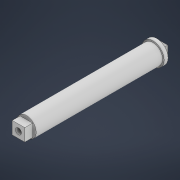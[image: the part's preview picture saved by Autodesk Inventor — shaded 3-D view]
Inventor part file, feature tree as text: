
AUTODESK INVENTOR PART (.ipt)
format: ipt  version: 2021 (Build 250183000, 183)  size: 122,880 bytes
history: native  units: mm
features: extrude x6, sketch x6
ambient origin geometry x8: Origin, YZ Plane, XZ Plane, XY Plane, X Axis, Y Axis, Z Axis, Center Point
bodies: Volumenkörper1 (feature_tree)
feature tree (12):
  extrude  "Extrusion1"  Depth=9.5mm
  extrude  "Extrusion2"  Depth=3.5mm
  extrude  "Extrusion3"  Depth=3.0mm
  extrude  "Extrusion4"  Depth=9.5mm
  extrude  "Extrusion5"  Depth=6.0mm
  extrude  "Extrusion6"  Depth=5.0mm
  sketch  "Skizze1"  dims[d0=9.5mm d1=9.5mm]
  sketch  "Skizze2"  dims[d2=3.5mm d3=0.0mm d4=17.0mm]
  sketch  "Skizze3"  dims[d5=3.0mm d6=0.0mm d7=14.8mm]
  sketch  "Skizze4"  dims[d8=96.0mm d9=0.0mm d10=9.5mm]
  sketch  "Skizze5"  dims[d11=6.0mm d12=0.0mm d13=4.5mm]
  sketch  "Skizze6"  dims[d14=5.0mm d15=0.0mm d16=4.5mm d17=5.0mm d18=0.0mm d19=1.1mm]
